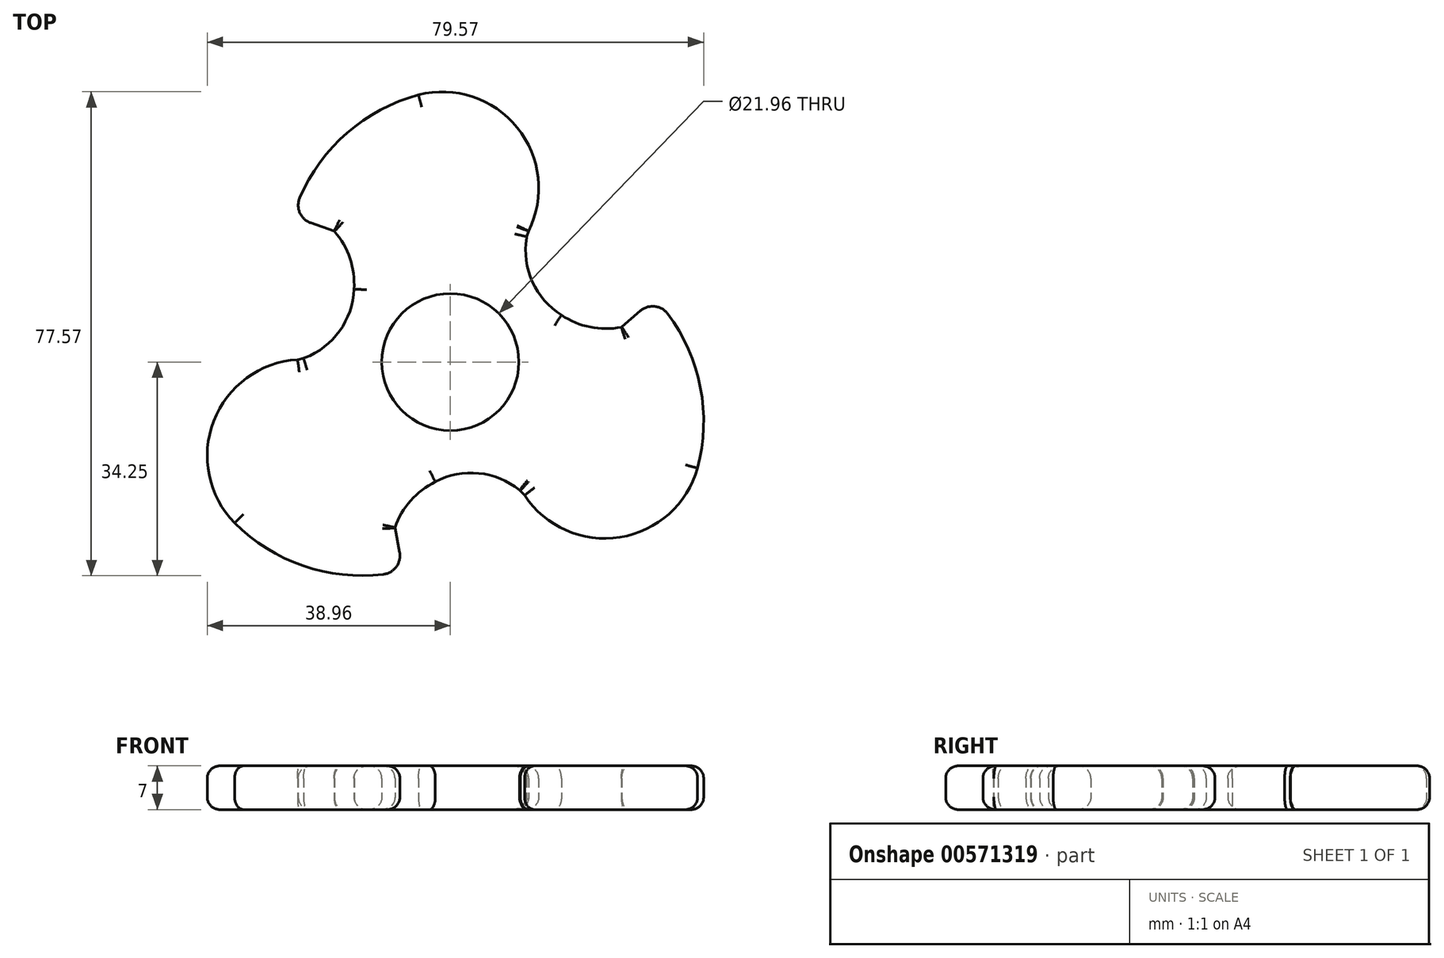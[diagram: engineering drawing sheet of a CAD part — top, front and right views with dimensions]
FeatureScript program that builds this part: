
annotation { "Feature Type Name" : "Feature", "Feature Type Description" : "" }
export const myFeature = defineFeature(function(context is Context, id is Id, definition is map)
    precondition{}
    {
        {
            var Q0;
            Q0=qCreatedBy(makeId("Top.planeOp"),FACE);
            var sketch = newSketch(context, id + "F0", { "sketchPlane" : qUnion([Q0])});
            skCircle(sketch, "E0", {"center": v(0, 0) * mm, "radius": 10.98 * mm});
            skPoint(sketch, "E1.start.orphan", {"position": v(0, 43.22) * mm});
            skPoint(sketch, "E2.2.0.end.orphan", {"position": v(32.77, 10.17) * mm});
            skPoint(sketch, "E3.orphan", {"position": v(11.11, -20.52) * mm});
            skPoint(sketch, "E4.trimOffspring.end.orphan", {"position": v(27.48, 5.59) * mm});
            skPoint(sketch, "E5.orphan", {"position": v(-8.9, -26.47) * mm});
            skPoint(sketch, "E6.orphan", {"position": v(-18.61, 21.02) * mm});
            skPoint(sketch, "E7.2.0", {"position": v(-23.33, 0.64) * mm});
            skArc(sketch, "E7.2.2", {"start": v(-23.36, 0.67) * mm, "mid": v(-17.74, 4.99) * mm, "end": v(-15.44, 11.7) * mm});
            skArc(sketch, "E7.2.3", {"start": v(-15.44, 11.7) * mm, "mid": v(-16.08, 16.63) * mm, "end": v(-18.56, 20.95) * mm});
            skLineSegment(sketch, "E7.2.4", {"start": v(-18.64, 21) * mm, "end": v(-25.23, 23.3) * mm});
            skLineSegment(sketch, "E7.2.5", {"start": v(-18.56, 20.95) * mm, "end": v(-18.64, 21) * mm});
            skArc(sketch, "E7.2.6", {"start": v(-5.1, 42.84) * mm, "mid": v(-17.7, 35.68) * mm, "end": v(-25.23, 23.3) * mm});
            skArc(sketch, "E7.2.7", {"start": v(12.54, 21) * mm, "mid": v(10.72, 37.58) * mm, "end": v(-5.1, 42.84) * mm});
            skPoint(sketch, "E8.orphan", {"position": v(12.77, 20.88) * mm});
            skPoint(sketch, "E9.1.3.end.orphan", {"position": v(-7.57, -33.47) * mm});
            skPoint(sketch, "E10.center", {"position": v(-0.02, -0.02) * mm});
            skPoint(sketch, "E11.orphan", {"position": v(12.23, 19.85) * mm});
            skPoint(sketch, "E12.orphan", {"position": v(32.77, 10.14) * mm});
            skLineSegment(sketch, "E13", {"start": v(-23.36, 0.67) * mm, "end": v(-23.52, 0.6) * mm});
            skPoint(sketch, "E14.orphan", {"position": v(-23.37, 0.63) * mm});
            skArc(sketch, "E15.1.2", {"start": v(11.1, -20.55) * mm, "mid": v(4.55, -17.84) * mm, "end": v(-2.4, -19.2) * mm});
            skArc(sketch, "E15.1.3", {"start": v(-2.4, -19.2) * mm, "mid": v(-6.36, -22.22) * mm, "end": v(-8.86, -26.52) * mm});
            skLineSegment(sketch, "E15.1.4", {"start": v(-8.87, -26.62) * mm, "end": v(-7.57, -33.48) * mm});
            skArc(sketch, "E15.1.5", {"start": v(-34.57, -25.8) * mm, "mid": v(-22.07, -33.15) * mm, "end": v(-7.57, -33.48) * mm});
            skArc(sketch, "E15.1.6", {"start": v(-24.49, 0.39) * mm, "mid": v(-37.93, -9.48) * mm, "end": v(-34.57, -25.8) * mm});
            skLineSegment(sketch, "E15.1.7", {"start": v(-24.49, 0.39) * mm, "end": v(-23.52, 0.6) * mm});
            skLineSegment(sketch, "E15.2.0", {"start": v(12.53, 20.98) * mm, "end": v(12.25, 20.09) * mm});
            skLineSegment(sketch, "E15.2.1", {"start": v(12.22, 19.9) * mm, "end": v(12.25, 20.09) * mm});
            skArc(sketch, "E15.2.2", {"start": v(12.22, 19.9) * mm, "mid": v(13.15, 12.87) * mm, "end": v(17.81, 7.52) * mm});
            skArc(sketch, "E15.2.3", {"start": v(17.81, 7.52) * mm, "mid": v(22.41, 5.6) * mm, "end": v(27.4, 5.59) * mm});
            skLineSegment(sketch, "E15.2.4", {"start": v(27.5, 5.63) * mm, "end": v(32.78, 10.18) * mm});
            skArc(sketch, "E15.2.5", {"start": v(39.63, -17.01) * mm, "mid": v(39.73, -2.53) * mm, "end": v(32.78, 10.18) * mm});
            skArc(sketch, "E15.2.6", {"start": v(11.9, -21.38) * mm, "mid": v(27.17, -28.09) * mm, "end": v(39.63, -17.01) * mm});
            skLineSegment(sketch, "E15.2.7", {"start": v(11.9, -21.38) * mm, "end": v(11.22, -20.63) * mm});
            skPoint(sketch, "E16.orphan", {"position": v(12.22, 19.89) * mm});
            skLineSegment(sketch, "E17", {"start": v(12.54, 21) * mm, "end": v(12.53, 20.98) * mm});
            skPoint(sketch, "E18.orphan", {"position": v(12.55, 21.05) * mm});
            skLineSegment(sketch, "E19", {"start": v(11.1, -20.55) * mm, "end": v(11.22, -20.63) * mm});
            skPoint(sketch, "E20.orphan", {"position": v(10.91, -20.39) * mm});
            skPoint(sketch, "E21.orphan", {"position": v(-23.11, 0.75) * mm});
            skPoint(sketch, "E22.orphan", {"position": v(-23.54, 0.6) * mm});
            skLineSegment(sketch, "E23", {"start": v(-8.86, -26.52) * mm, "end": v(-8.87, -26.62) * mm});
            skLineSegment(sketch, "E24", {"start": v(27.4, 5.59) * mm, "end": v(27.5, 5.63) * mm});
            skSolve(sketch);
        }
        {
            var Q0;
            Q0=qSketchRegion(id+"F0",true);
            extrude(context, id + "F1", {"entities" : qUnion([Q0]), "depth" : 7 * mm, "offsetDistance" : 25 * mm});
        }
        {
            var Q0;
            Q0=makeQuery(id+"F1.opExtrude","CAP_FACE",FACE,{"disambiguationData":[OSD([sQuery(id+"F0.wireOp",EDGE,"E0"),sQuery(id+"F0.wireOp",EDGE,"9wtZnRUA-MULs-dOer-4M8c-Zti45ueDNHAE"),sQuery(id+"F0.wireOp",EDGE,"bfb47979-994e-4c35-8f3f-2d9462ef9953.1.0"),sQuery(id+"F0.wireOp",EDGE,"bfb47979-994e-4c35-8f3f-2d9462ef9953.2.0"),sQuery(id+"F0.wireOp",EDGE,"E9.1.0"),sQuery(id+"F0.wireOp",EDGE,"E9.1.1"),sQuery(id+"F0.wireOp",EDGE,"E9.1.2"),sQuery(id+"F0.wireOp",EDGE,"E9.1.3"),sQuery(id+"F0.wireOp",EDGE,"E9.1.4"),sQuery(id+"F0.wireOp",EDGE,"MSOVAvHY-2dng-qJIN-EstG-JEKkyfnc06y0"),sQuery(id+"F0.wireOp",EDGE,"Qhv8092y-Y5Qe-Pu52-p0u7-aBsJBwILmqKw"),sQuery(id+"F0.wireOp",EDGE,"E7.1.2"),sQuery(id+"F0.wireOp",EDGE,"E7.1.3"),sQuery(id+"F0.wireOp",EDGE,"E7.1.4"),sQuery(id+"F0.wireOp",EDGE,"E7.1.5"),sQuery(id+"F0.wireOp",EDGE,"E7.1.6"),sQuery(id+"F0.wireOp",EDGE,"E7.1.7"),sQuery(id+"F0.wireOp",EDGE,"E7.1.8"),sQuery(id+"F0.wireOp",EDGE,"E7.2.2"),sQuery(id+"F0.wireOp",EDGE,"E7.2.3"),sQuery(id+"F0.wireOp",EDGE,"E7.2.4"),sQuery(id+"F0.wireOp",EDGE,"E7.2.5"),sQuery(id+"F0.wireOp",EDGE,"E7.2.6"),sQuery(id+"F0.wireOp",EDGE,"E7.2.7"),sQuery(id+"F0.wireOp",EDGE,"E7.2.8")])],"isStart":false});
            var Q1;
            Q1=makeQuery(id+"F1.opExtrude","CAP_FACE",FACE,{"disambiguationData":[OSD([sQuery(id+"F0.wireOp",EDGE,"E0"),sQuery(id+"F0.wireOp",EDGE,"9wtZnRUA-MULs-dOer-4M8c-Zti45ueDNHAE"),sQuery(id+"F0.wireOp",EDGE,"bfb47979-994e-4c35-8f3f-2d9462ef9953.1.0"),sQuery(id+"F0.wireOp",EDGE,"bfb47979-994e-4c35-8f3f-2d9462ef9953.2.0"),sQuery(id+"F0.wireOp",EDGE,"E7.1.5"),sQuery(id+"F0.wireOp",EDGE,"E7.2.2"),sQuery(id+"F0.wireOp",EDGE,"E7.2.3"),sQuery(id+"F0.wireOp",EDGE,"E7.2.4"),sQuery(id+"F0.wireOp",EDGE,"E7.2.5"),sQuery(id+"F0.wireOp",EDGE,"E7.2.6"),sQuery(id+"F0.wireOp",EDGE,"E7.2.7"),sQuery(id+"F0.wireOp",EDGE,"wI4vbt6F-0did-M85L-NOSj-vaBcgqnXykCr"),sQuery(id+"F0.wireOp",EDGE,"E10.1.0"),sQuery(id+"F0.wireOp",EDGE,"E10.1.1"),sQuery(id+"F0.wireOp",EDGE,"E10.1.2"),sQuery(id+"F0.wireOp",EDGE,"E10.1.3"),sQuery(id+"F0.wireOp",EDGE,"E10.1.4"),sQuery(id+"F0.wireOp",EDGE,"E10.1.5"),sQuery(id+"F0.wireOp",EDGE,"E10.2.0"),sQuery(id+"F0.wireOp",EDGE,"E10.2.1"),sQuery(id+"F0.wireOp",EDGE,"E10.2.2"),sQuery(id+"F0.wireOp",EDGE,"E10.2.3"),sQuery(id+"F0.wireOp",EDGE,"E10.2.4"),sQuery(id+"F0.wireOp",EDGE,"E10.2.5"),sQuery(id+"F0.wireOp",EDGE,"rdTHZh58-hr0x-KPgI-GlKq-AtTTfWVPiPXA")])],"isStart":true});
            fillet(context, id + "F2", {"entities" : qUnion([Q0, Q1]), "radius" : 2 * mm, "tangentPropagation" : true, "allowEdgeOverflow" : false});
        }
        {
            var Q0;
            Q0=makeQuery(id+"F1.opExtrude","SWEPT_EDGE",EDGE,{"disambiguationData":[OSD([sQuery(id+"F0.wireOp",EDGE,"E7.1.4"),sQuery(id+"F0.wireOp",EDGE,"E7.1.6")])]});
            var Q1;
            Q1=makeQuery(id+"F1.opExtrude","SWEPT_EDGE",EDGE,{"disambiguationData":[OSD([sQuery(id+"F0.wireOp",EDGE,"E7.2.4"),sQuery(id+"F0.wireOp",EDGE,"E7.2.6")])]});
            var Q2;
            Q2=makeQuery(id+"F1.opExtrude","SWEPT_EDGE",EDGE,{"disambiguationData":[OSD([sQuery(id+"F0.wireOp",EDGE,"E9.1.2"),sQuery(id+"F0.wireOp",EDGE,"E9.1.3")])]});
            var Q3;
            Q3=makeQuery(id+"F1.opExtrude","SWEPT_EDGE",EDGE,{"disambiguationData":[OSD([sQuery(id+"F0.wireOp",EDGE,"E10.2.2"),sQuery(id+"F0.wireOp",EDGE,"E10.2.3")])]});
            var Q4;
            Q4=makeQuery(id+"F1.opExtrude","SWEPT_EDGE",EDGE,{"disambiguationData":[OSD([sQuery(id+"F0.wireOp",EDGE,"E10.1.2"),sQuery(id+"F0.wireOp",EDGE,"E10.1.3")])]});
            var Q5;
            Q5=makeQuery(id+"F1.opExtrude","SWEPT_EDGE",EDGE,{"disambiguationData":[OSD([sQuery(id+"F0.wireOp",EDGE,"E15.2.4"),sQuery(id+"F0.wireOp",EDGE,"E15.2.5")])]});
            var Q6;
            Q6=makeQuery(id+"F1.opExtrude","SWEPT_EDGE",EDGE,{"disambiguationData":[OSD([sQuery(id+"F0.wireOp",EDGE,"E15.1.4"),sQuery(id+"F0.wireOp",EDGE,"E15.1.5")])]});
            fillet(context, id + "F3", {"entities" : qUnion([Q0, Q1, Q2, Q3, Q4, Q5, Q6]), "radius" : 3 * mm, "tangentPropagation" : true, "allowEdgeOverflow" : false});
        }
    });
